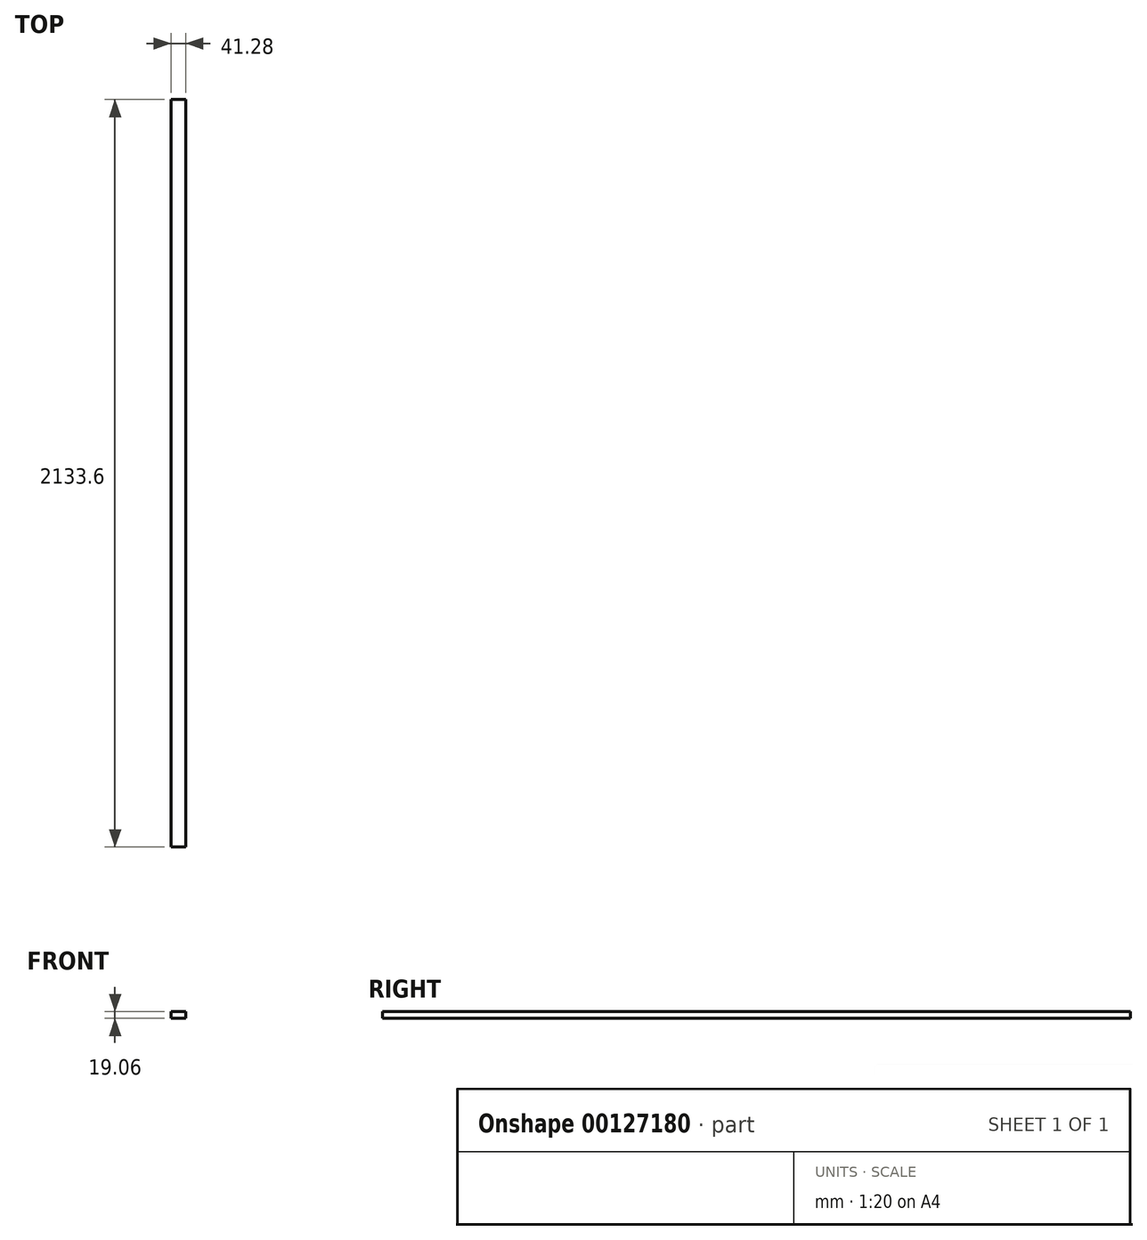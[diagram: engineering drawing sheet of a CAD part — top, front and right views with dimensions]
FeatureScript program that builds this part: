
annotation { "Feature Type Name" : "Feature", "Feature Type Description" : "" }
export const myFeature = defineFeature(function(context is Context, id is Id, definition is map)
    precondition{}
    {
        {
            var Q0;
            Q0=qCreatedBy(makeId("Front.planeOp"),FACE);
            var sketch = newSketch(context, id + "F0", { "sketchPlane" : qUnion([Q0])});
            skLineSegment(sketch, "E0.bottom", {"start": v(20.64, -9.52) * mm, "end": v(-20.64, -9.52) * mm});
            skLineSegment(sketch, "E0.top", {"start": v(20.64, 9.53) * mm, "end": v(-20.64, 9.53) * mm});
            skLineSegment(sketch, "E0.left", {"start": v(20.64, -9.52) * mm, "end": v(20.64, 9.53) * mm});
            skLineSegment(sketch, "E0.right", {"start": v(-20.64, -9.52) * mm, "end": v(-20.64, 9.53) * mm});
            skPoint(sketch, "E0.middle", {"position": v(0, 0) * mm});
            skSolve(sketch);
        }
        {
            var Q0;
            Q0=qSketchRegion(id+"F0",true);
            extrude(context, id + "F1", {"entities" : qUnion([Q0]), "depth" : 2133.6 * mm});
        }
    });
